# Revit family: Deca_Caixa de descarga embutida para drywall para bacia suspensa_Caixa embutida Hydra_2502.CX.AF
name_source: partatom
category: Plumbing Fixtures
units: mm (PartAtom-declared; Revit-internal decimal feet)

## family parameters
Cut with Voids When Loaded = Yes
Host = Face
Part Type = Normal
Room Calculation Point = No
Round Connector Dimension = Use Radius
Shared = No

## types (2) — shared parameters
Acompanha o Produto = Acompanha varão para fixação do vaso; porcas e arruelas para fixação do vaso;  acabamento para as porcas; spud e canopla; Conexão para esgoto; suporte com chumbadores para fixação no piso
Aprovado por = quattroD
Atendimento ao Cliente = 0800-0117073
Categoria = SISTEMAS DE DESCARGA
Composição Anel Vedação = -
Composição Assento = -
Composição Básica = Liga de Cobre (bronze e latão),Plásticos de Engenharia,Elastômeros
Composição Componente = -
Consumo = 6 / 3 (lpf) - 1,6 / 0,8 (gpf)
Cor Interna = -
Cor Principal = Não Possui
Cor Secundária = -
Cores Componente = -
Criado por = quattroD
Código Pai = 2502.CX.AF
Description = Caixa de descarga embutida para drywall para bacia suspensa
Diâmetro Ponto de Esgoto = 100 mm  [stored 0.328084 ft]
Diâmetro Água Fria = 15 mm  [stored 0.0492126 ft]
Diâmetro Água Fria Saída = 40 mm  [stored 0.131234 ft]
Informações Complementares = -
Itens de Instalação = 4900.C.HPR.DUO; 4900.C.HSL.DUO; 4900.E.HSL.DUO.BR
Linha = Caixa embutida Hydra
Manufacturer = Deca
Norma = NBR15491
Pressão máx. funcionamento = 40 MCA
Pressão mín. Aquec. Acúmulo = -
Pressão mín. Aquec. Passagem = -
Pressão mín. funcionamento = 2 MCA
Raio Ponto de Esgoto = 50 mm  [stored 0.164042 ft]
Raio Água Fria = 8 mm  [stored 0.0262467 ft]
Raio Água Fria Saída = 20 mm  [stored 0.0656168 ft]
Saída de Esgoto = -
Segmento = Válvula Hydra
Tipo de dispositivo economizador = -
Tipo de mecanismo utilizado = -
Tipo de rosca de entrada = BSP NBR 8133
Tipo de rosca de saída = BSP NBR 8133
URL = www.deca.com.br
Vazão na Pressão máx. (L/min) = -
Vazão na Pressão mín. (L/min) = -
zero-valued in all types: Default Elevation

## per-type parameters (varying)
| type | Peso Líquido (Kg) | Visibilidade Mecanismo Interno |
| 2502.CX.PN.AF | 6 | Yes |
| 2502.CX.MC.AF | 14.8 | No |

note: column(s) folded — value = type name in every type: Model

note: [stored X ft] marks values corroborated as IEEE doubles in the binary element streams (Revit-internal decimal feet)

## geometry (parser evidence)
native form markers: Sweep x3
no freeform markers — native parametric forms only
